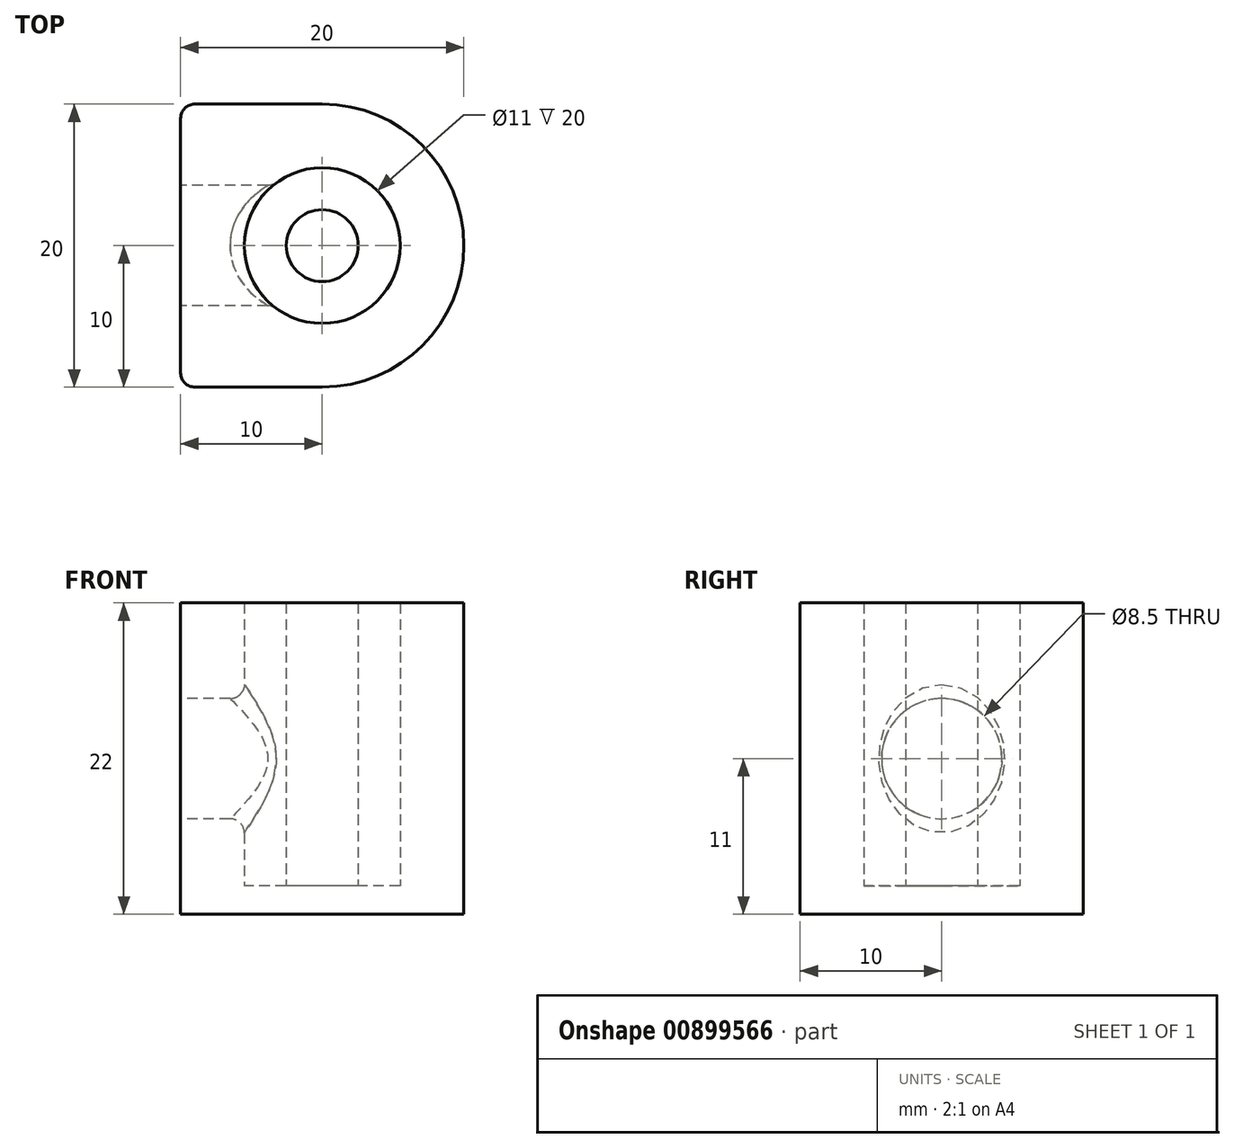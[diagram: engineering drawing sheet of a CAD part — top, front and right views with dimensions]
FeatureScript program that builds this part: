
annotation { "Feature Type Name" : "Feature", "Feature Type Description" : "" }
export const myFeature = defineFeature(function(context is Context, id is Id, definition is map)
    precondition{}
    {
        {
            var Q0;
            Q0=qCreatedBy(makeId("Top.planeOp"),FACE);
            var sketch = newSketch(context, id + "F0", { "sketchPlane" : qUnion([Q0])});
            skCircle(sketch, "E0", {"center": v(0, 0) * mm, "radius": 5.5 * mm});
            skArc(sketch, "E1", {"start": v(0, -10) * mm, "mid": v(10, 0) * mm, "end": v(0, 10) * mm});
            skLineSegment(sketch, "E2", {"start": v(0, 10) * mm, "end": v(-10, 10) * mm});
            skLineSegment(sketch, "E3", {"start": v(0, -10) * mm, "end": v(-10, -10) * mm});
            skLineSegment(sketch, "E4", {"start": v(-10, -10) * mm, "end": v(-10, 10) * mm});
            skCircle(sketch, "E5", {"center": v(0, 0) * mm, "radius": 2.54 * mm});
            skSolve(sketch);
        }
        {
            var Q0;
            Q0=makeQuery(id+"F0.imprint","IMPRINT",FACE,{"disambiguationData":[TD([[makeQuery(id+"F0.imprint","IMPRINT",EDGE,{"derivedFrom":sQuery(id+"F0.wireOp",EDGE,"E0")}),-1.0]])]});
            extrude(context, id + "F1", {"entities" : qUnion([Q0]), "depth" : 22 * mm, "offsetDistance" : 25 * mm});
        }
        {
            var Q0;
            Q0=makeQuery(id+"F0.imprint","IMPRINT",FACE,{"disambiguationData":[TD([[makeQuery(id+"F0.imprint","IMPRINT",EDGE,{"derivedFrom":sQuery(id+"F0.wireOp",EDGE,"E0")}),1.0]])]});
            extrude(context, id + "F2", {"entities" : qUnion([Q0]), "operationType" : NewBodyOperationType.ADD, "depth" : 2 * mm, "offsetDistance" : 25 * mm});
        }
        {
            var Q0;
            Q0=makeQuery(id+"F1.opExtrude","SWEPT_FACE",FACE,{"disambiguationData":[OSD([sQuery(id+"F0.wireOp",EDGE,"E4")])]});
            var sketch = newSketch(context, id + "F3", { "sketchPlane" : qUnion([Q0])});
            skLineSegment(sketch, "E6", {"start": v(10, 22) * mm, "end": v(-10, 0) * mm, "construction": true});
            skLineSegment(sketch, "E7", {"start": v(-10, 22) * mm, "end": v(10, 0) * mm, "construction": true});
            skCircle(sketch, "E8", {"center": v(0, 11) * mm, "radius": 4.25 * mm});
            skSolve(sketch);
        }
        {
            var Q0;
            Q0=makeQuery(id+"F3.imprint","IMPRINT",FACE,{"disambiguationData":[TD([[makeQuery(id+"F3.imprint","IMPRINT",EDGE,{"derivedFrom":sQuery(id+"F3.wireOp",EDGE,"E8")}),1.0]])]});
            extrude(context, id + "F4", {"entities" : qUnion([Q0]), "operationType" : NewBodyOperationType.REMOVE, "oppositeDirection" : true, "depth" : 10 * mm, "offsetDistance" : 25 * mm});
        }
        {
            var Q0;
            Q0=makeQuery(id+"F0.imprint","IMPRINT",FACE,{"disambiguationData":[TD([[makeQuery(id+"F0.imprint","IMPRINT",EDGE,{"derivedFrom":sQuery(id+"F0.wireOp",EDGE,"E5")}),1.0]])]});
            var Q1;
            Q1=sQuery(id+"F0.wireOp",EDGE,"E5");
            extrude(context, id + "F5", {"entities" : qUnion([Q0]), "operationType" : NewBodyOperationType.ADD, "surfaceEntities" : qUnion([Q1]), "depth" : 22 * mm, "offsetDistance" : 25 * mm});
        }
        {
            var Q0;
            Q0=makeQuery(id+"F1.opExtrude","SWEPT_EDGE",EDGE,{"disambiguationData":[OSD([sQuery(id+"F0.wireOp",EDGE,"E3"),sQuery(id+"F0.wireOp",EDGE,"E4")])]});
            var Q1;
            Q1=makeQuery(id+"F1.opExtrude","SWEPT_EDGE",EDGE,{"disambiguationData":[OSD([sQuery(id+"F0.wireOp",EDGE,"E2"),sQuery(id+"F0.wireOp",EDGE,"E4")])]});
            var Q2;
            Q2=makeQuery(id+"F4.boolean.opBoolean","INTERSECT",EDGE,{"derivedFrom":[makeQuery(id+"F1.opExtrude","SWEPT_FACE",FACE,{"disambiguationData":[OSD([sQuery(id+"F0.wireOp",EDGE,"E0")])]}),makeQuery(id+"F4.opExtrude","SWEPT_FACE",FACE,{"disambiguationData":[OSD([sQuery(id+"F3.wireOp",EDGE,"E8")])]})]});
            fillet(context, id + "F6", {"entities" : qUnion([Q0, Q1, Q2]), "radius" : 1 * mm, "tangentPropagation" : true, "allowEdgeOverflow" : false});
        }
    });
